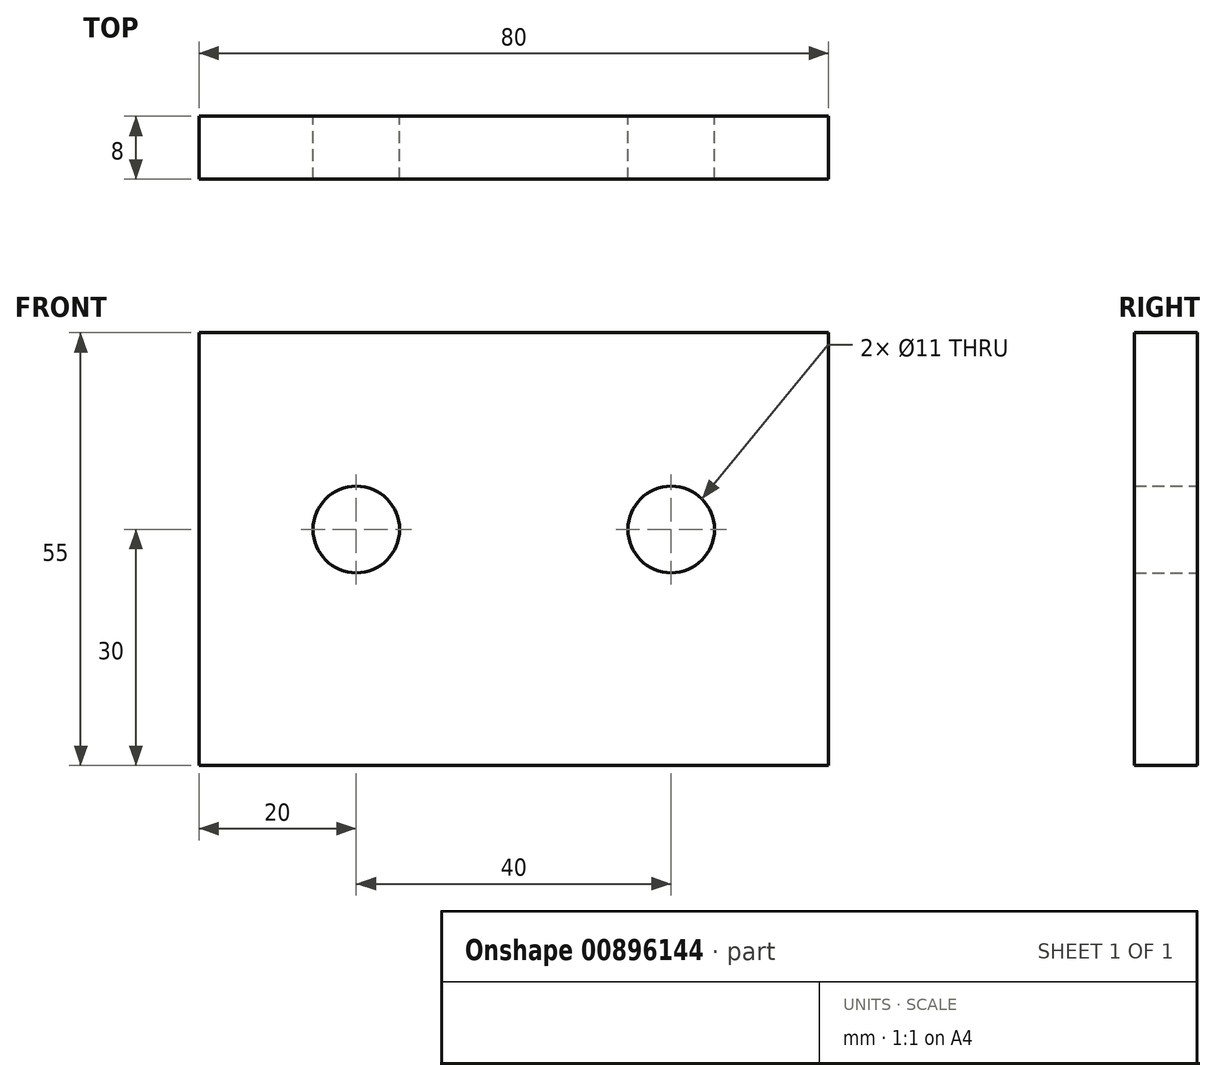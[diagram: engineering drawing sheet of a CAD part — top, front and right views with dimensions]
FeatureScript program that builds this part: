
annotation { "Feature Type Name" : "Feature", "Feature Type Description" : "" }
export const myFeature = defineFeature(function(context is Context, id is Id, definition is map)
    precondition{}
    {
        {
            var Q0;
            Q0=qCreatedBy(makeId("Front.planeOp"),FACE);
            var sketch = newSketch(context, id + "F0", { "sketchPlane" : qUnion([Q0])});
            skLineSegment(sketch, "E0.bottom", {"start": v(40, 27.5) * mm, "end": v(-40, 27.5) * mm});
            skLineSegment(sketch, "E0.top", {"start": v(40, -27.5) * mm, "end": v(-40, -27.5) * mm});
            skLineSegment(sketch, "E0.left", {"start": v(40, 27.5) * mm, "end": v(40, -27.5) * mm});
            skLineSegment(sketch, "E0.right", {"start": v(-40, 27.5) * mm, "end": v(-40, -27.5) * mm});
            skPoint(sketch, "E0.middle", {"position": v(0, 0) * mm});
            skCircle(sketch, "E1", {"center": v(-20, 2.5) * mm, "radius": 5.5 * mm});
            skCircle(sketch, "E2", {"center": v(20, 2.5) * mm, "radius": 5.5 * mm});
            skSolve(sketch);
        }
        {
            var Q0;
            Q0=makeQuery(id+"F0.imprint","IMPRINT",FACE,{"disambiguationData":[TD([[makeQuery(id+"F0.imprint","IMPRINT",EDGE,{"derivedFrom":sQuery(id+"F0.wireOp",EDGE,"E0.bottom")}),1.0]])]});
            extrude(context, id + "F1", {"entities" : qUnion([Q0]), "depth" : 8 * mm, "offsetDistance" : 25 * mm});
        }
    });
